# Revit family: Paper_Holder-GROHE-Seabury-40160_Series
name_source: partatom
category: Generic Models
revit_build: Autodesk Revit 2014 (Build: 20130308_1515(x64)
units: mm (PartAtom-declared; Revit-internal decimal feet)

## types (4) — shared parameters
Assembly Code = D2010710
Default Elevation = 24"
Description = Seabury Toilet paper holder
Height = 3 7/8"
Installation Type = Wall Mounted
Length = 3 5/8"
Manufacturer = Grohe
Price = Prices may vary. Please consult Manufacturer Representative for most up-to-date price list.
Product Page URL = https://www.grohe.ca
URL = https://www.grohe.com
Warranty Documentation Link = https://cdn.cloud.grohe.com
Width = 5 5/8"

## per-type parameters (varying)
| type | Finish | Material | Shipping Weight |
| 40160000 | Metal-Grohe-000-Chrome | Metal-Grohe-000-Chrome | 1.102 lb |
| 40160EN0 | Metal-Grohe-EN0-Brushed Nickel | Metal-Grohe-EN0-Brushed Nickel | 1.609 lb |
| 40160BE0 | Metal-Grohe-BE0-Nickel | Metal-Grohe-BE0-Nickel | 1.609 lb |
| 40160ZB0 | Metal-Grohe-ZB0-Oil Rubbed Bronze | Metal-Grohe-ZB0-Oil Rubbed Bronze | 1.609 lb |

note: column(s) folded — value = type name in every type: Model

## geometry (parser evidence)
native form markers: Sweep x3
no freeform markers — native parametric forms only
